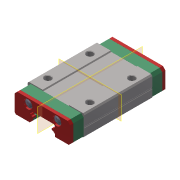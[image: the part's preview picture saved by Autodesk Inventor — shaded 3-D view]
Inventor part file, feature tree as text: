
AUTODESK INVENTOR PART (.ipt)
format: ipt  version: 2019.4 (Build 234330000, 330)  size: 465,920 bytes
history: imported  units: mm
features: other x9, plane x2, imported_body x1
ambient origin geometry x8: Origin, YZ Plane, XZ Plane, XY Plane, X Axis, Y Axis, Z Axis, Center Point
bodies: Solid1 (imported_parasolid), Solid2 (imported_parasolid), Solid3 (imported_parasolid), Solid4 (imported_parasolid), Solid5 (imported_parasolid), Solid6 (imported_parasolid), Solid7 (imported_parasolid), Solid8 (imported_parasolid), Solid9 (imported_parasolid)
feature tree (12):
  plane  "Work Plane1"
  plane  "Work Plane2"
  other  "MID BODY, MGN 12H, LINEAR GUIDE BLOCK-1-solid1"
  other  "MID BODY, MGN 12H, LINEAR GUIDE BLOCK-1-solid2"
  other  "MID BODY, MGN 12H, LINEAR GUIDE BLOCK-1-solid3"
  other  "MID BODY, MGN 12H, LINEAR GUIDE BLOCK-1-solid4"
  other  "MID BODY, MGN 12H, LINEAR GUIDE BLOCK-1-solid5"
  other  "SCREW HEAD, MGN 12H, LINEAR GUIDE BLOCK-1-solid1"
  other  "SCREW HEAD, MGN 12H, LINEAR GUIDE BLOCK-2-solid1"
  other  "SCREW HEAD, MGN 12H, LINEAR GUIDE BLOCK-3-solid1"
  other  "SCREW HEAD, MGN 12H, LINEAR GUIDE BLOCK-4-solid1"
  imported_body  NMx_Import_Brep_tag  [imported B-rep: ~50 faces, bbox_mm=[19.044812, 8.226555, 32.4]]
